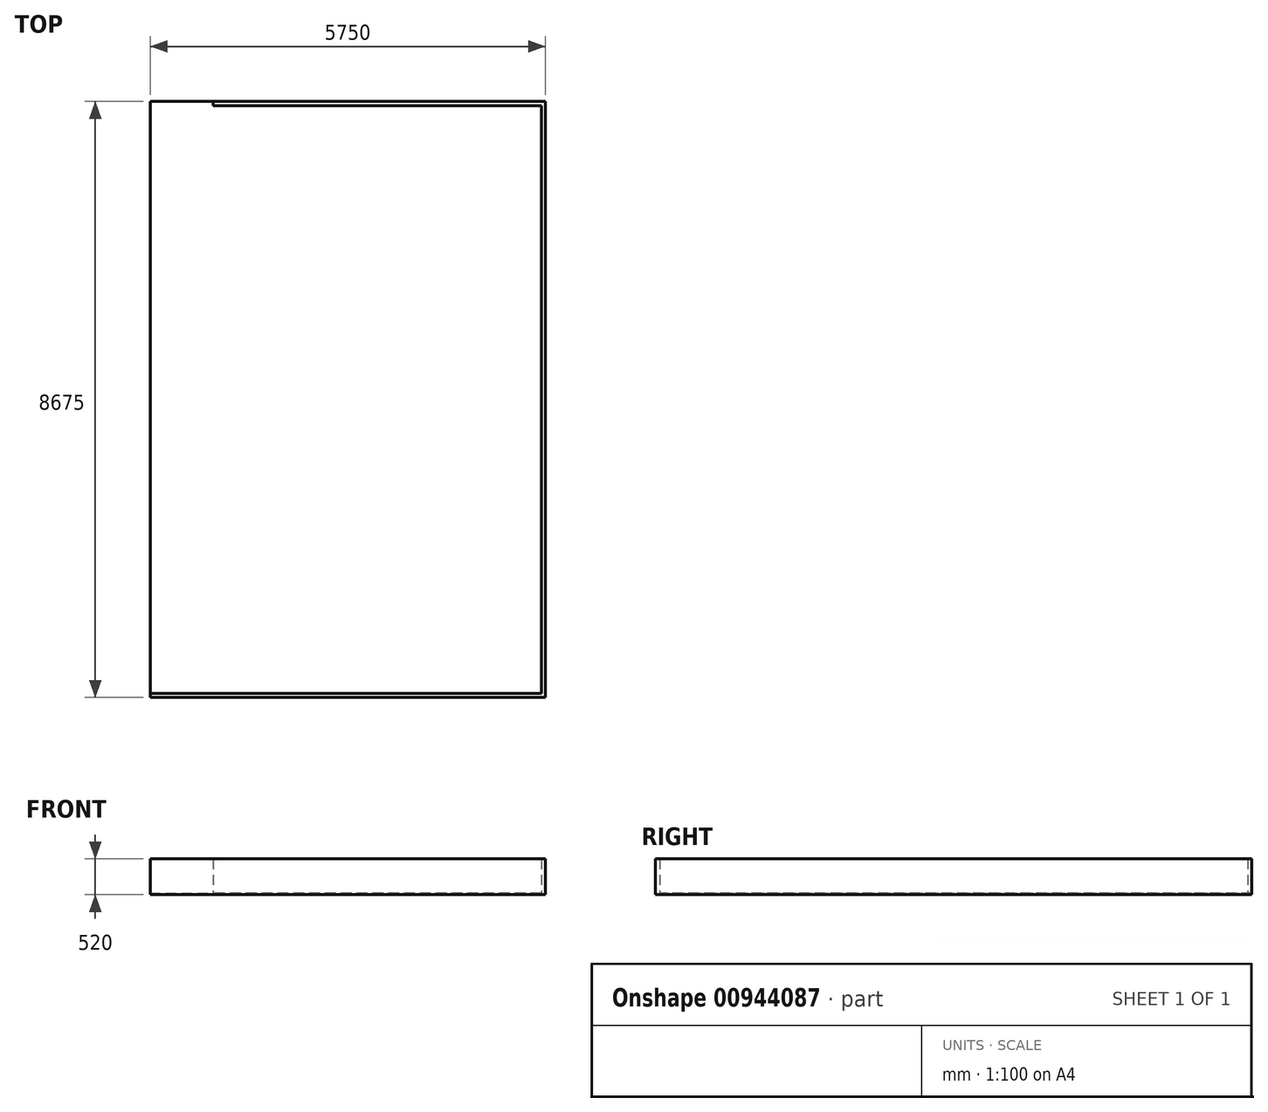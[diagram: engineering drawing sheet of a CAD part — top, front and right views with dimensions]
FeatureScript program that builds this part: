
annotation { "Feature Type Name" : "Feature", "Feature Type Description" : "" }
export const myFeature = defineFeature(function(context is Context, id is Id, definition is map)
    precondition{}
    {
        {
            var Q0;
            Q0=qCreatedBy(makeId("Top.planeOp"),FACE);
            var sketch = newSketch(context, id + "F0", { "sketchPlane" : qUnion([Q0])});
            skLineSegment(sketch, "E0.bottom", {"start": v(-2875, 4337.5) * mm, "end": v(2875, 4337.5) * mm});
            skLineSegment(sketch, "E0.top", {"start": v(-2875, -4337.5) * mm, "end": v(2875, -4337.5) * mm});
            skLineSegment(sketch, "E0.left", {"start": v(-2875, 4337.5) * mm, "end": v(-2875, -4337.5) * mm});
            skLineSegment(sketch, "E0.right", {"start": v(2875, 4337.5) * mm, "end": v(2875, -4337.5) * mm});
            skPoint(sketch, "E0.middle", {"position": v(0, 0) * mm});
            skLineSegment(sketch, "E1", {"start": v(2875, 4529.73) * mm, "end": v(-2215, 4529.73) * mm});
            skLineSegment(sketch, "E2", {"start": v(-2215, 4337.5) * mm, "end": v(-2215, 4529.73) * mm});
            skLineSegment(sketch, "E3", {"start": v(-2215, 4337.5) * mm, "end": v(-2875, 3543.1) * mm});
            skSolve(sketch);
        }
        {
            var Q0;
            Q0 = qSketchRegion(id + "F0", true);
            extrude(context, id + "F1", {"entities" : qUnion([Q0]), "depth" : 20 * mm, "offsetDistance" : 25 * mm});
        }
        {
            var Q0;
            Q0=makeQuery(id+"F1.opExtrude","CAP_FACE",FACE,{"disambiguationData":[OSD([sQuery(id+"F0.wireOp",EDGE,"E0.bottom"),sQuery(id+"F0.wireOp",EDGE,"E0.top"),sQuery(id+"F0.wireOp",EDGE,"E0.left"),sQuery(id+"F0.wireOp",EDGE,"E0.right")])],"isStart":false});
            var sketch = newSketch(context, id + "F2", { "sketchPlane" : qUnion([Q0])});
            skLineSegment(sketch, "E4", {"start": v(-1958.81, 4337.5) * mm, "end": v(2875, 4337.5) * mm});
            skLineSegment(sketch, "E5", {"start": v(2875, 4337.5) * mm, "end": v(2875, -4337.5) * mm});
            skLineSegment(sketch, "E6", {"start": v(2875, -4337.5) * mm, "end": v(-2875, -4337.5) * mm});
            skLineSegment(sketch, "E7", {"start": v(-2875, -4337.5) * mm, "end": v(-2875, -4277.5) * mm});
            skLineSegment(sketch, "E8", {"start": v(-2875, -4277.5) * mm, "end": v(2815, -4277.5) * mm});
            skLineSegment(sketch, "E9", {"start": v(2815, -4277.5) * mm, "end": v(2815, 4277.5) * mm});
            skLineSegment(sketch, "E10", {"start": v(2815, 4277.5) * mm, "end": v(-1958.81, 4277.5) * mm});
            skLineSegment(sketch, "E11", {"start": v(-1958.81, 4277.5) * mm, "end": v(-1958.81, 4337.5) * mm});
            skSolve(sketch);
        }
        {
            var Q0;
            Q0 = qSketchRegion(id + "F2", true);
            extrude(context, id + "F3", {"entities" : qUnion([Q0]), "operationType" : NewBodyOperationType.ADD, "depth" : 500 * mm, "offsetDistance" : 25 * mm});
        }
    });
